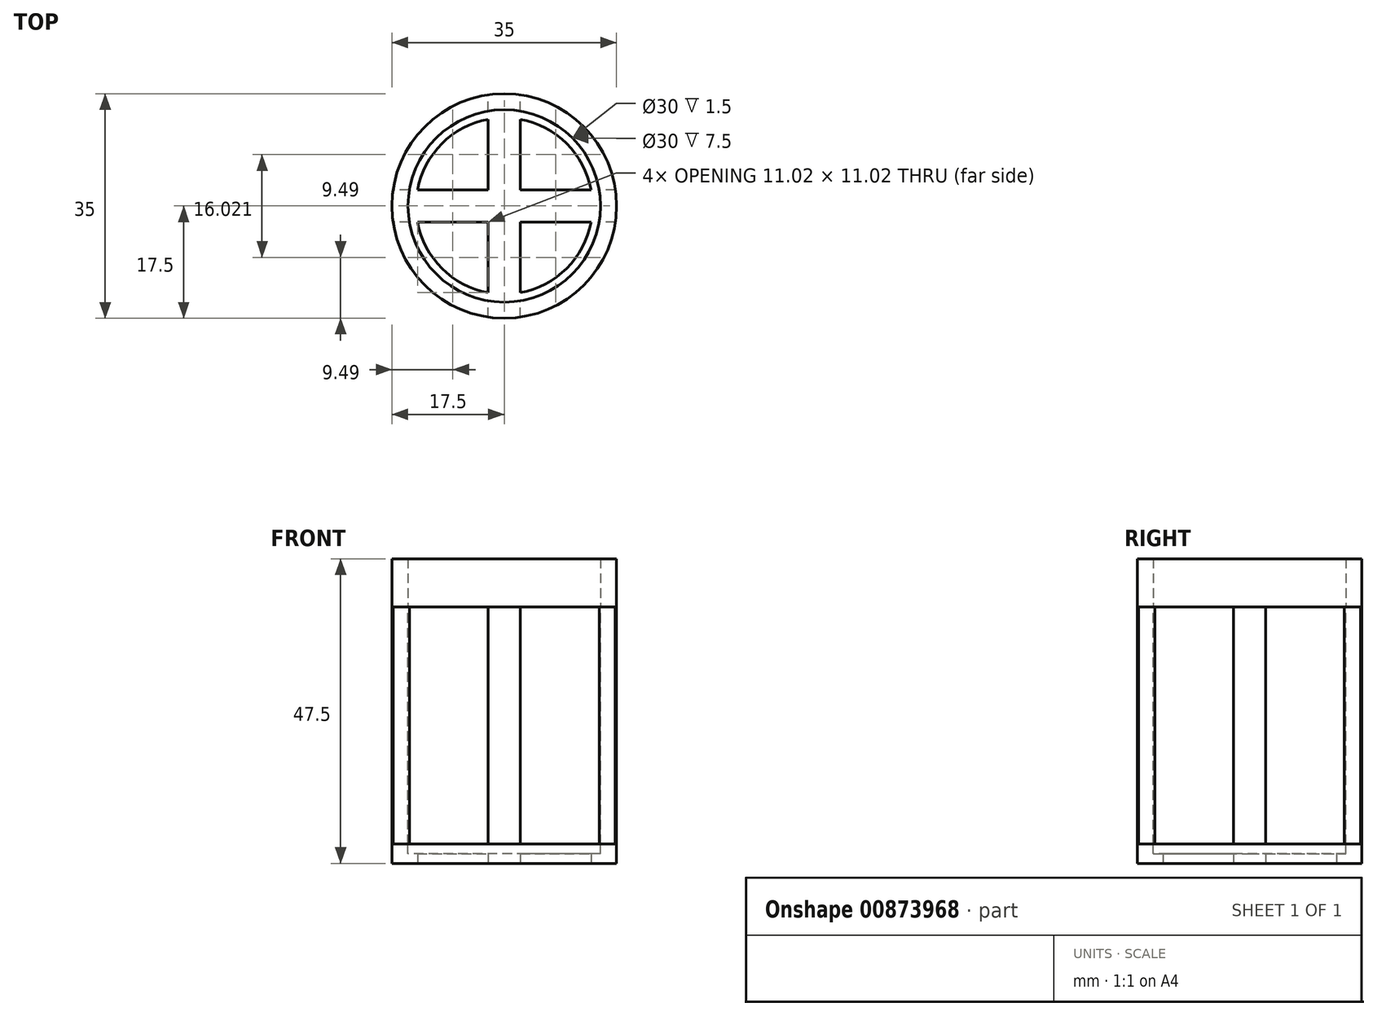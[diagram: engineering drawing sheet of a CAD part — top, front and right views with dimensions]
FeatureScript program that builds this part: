
annotation { "Feature Type Name" : "Feature", "Feature Type Description" : "" }
export const myFeature = defineFeature(function(context is Context, id is Id, definition is map)
    precondition{}
    {
        {
            var Q0;
            Q0=qCreatedBy(makeId("Top.planeOp"),FACE);
            var sketch = newSketch(context, id + "F0", { "sketchPlane" : qUnion([Q0])});
            skPoint(sketch, "E0.first.point", {"position": v(0, 0) * mm});
            skCircle(sketch, "E1", {"center": v(0, 0) * mm, "radius": 17.5 * mm});
            skCircle(sketch, "E2", {"center": v(0, 0) * mm, "radius": 13.75 * mm});
            skSolve(sketch);
        }
        {
            var Q0;
            Q0=makeQuery(id+"F0.imprint","IMPRINT",FACE,{"disambiguationData":[TD([[makeQuery(id+"F0.imprint","IMPRINT",EDGE,{"derivedFrom":sQuery(id+"F0.wireOp",EDGE,"E1")}),1.0]])]});
            extrude(context, id + "F1", {"entities" : qUnion([Q0]), "depth" : 43 * mm, "offsetDistance" : 25 * mm});
        }
        {
            var Q0;
            Q0=makeQuery(id+"F1.opExtrude","CAP_FACE",FACE,{"disambiguationData":[OSD([sQuery(id+"F0.wireOp",EDGE,"dMLi9CjI-w3AJ-lqrU-xDtC-pNT5ZKXLwRoQ"),sQuery(id+"F0.wireOp",EDGE,"p6jEfgZd-gn9l-At6D-uO4C-P7PHmhyGIQ6Y"),sQuery(id+"F0.wireOp",EDGE,"bsXDQPTp-62U9-H9b8-tNQK-BlYfqYmaa6Ta"),sQuery(id+"F0.wireOp",EDGE,"E1")])],"isStart":false});
            var sketch = newSketch(context, id + "F2", { "sketchPlane" : qUnion([Q0])});
            skCircle(sketch, "E3", {"center": v(0, 0) * mm, "radius": 15 * mm});
            skCircle(sketch, "E4", {"center": v(0, 0) * mm, "radius": 13.75 * mm});
            skSolve(sketch);
        }
        {
            var Q0;
            Q0 = qSketchRegion(id + "F2", true);
            extrude(context, id + "F3", {"entities" : qUnion([Q0]), "operationType" : NewBodyOperationType.REMOVE, "oppositeDirection" : true, "depth" : 41.5 * mm, "offsetDistance" : 25 * mm});
        }
        {
            var Q0;
            Q0=qCreatedBy(makeId("Top.planeOp"),FACE);
            cPlane(context, id + "F4", {"entities" : qUnion([Q0]), "cplaneType" : CPlaneType.OFFSET, "offset" : 3 * mm, "width" : 150 * mm, "height" : 150 * mm});
        }
        {
            var Q0;
            Q0=qCreatedBy(id+"F4.planeOp",FACE);
            var sketch = newSketch(context, id + "F5", { "sketchPlane" : qUnion([Q0])});
            skLineSegment(sketch, "E5.bottom", {"start": v(36.84, 2.5) * mm, "end": v(-36.84, 2.5) * mm});
            skLineSegment(sketch, "E5.top", {"start": v(36.84, -2.5) * mm, "end": v(-36.84, -2.5) * mm});
            skLineSegment(sketch, "E5.left", {"start": v(36.84, 2.5) * mm, "end": v(36.84, -2.5) * mm});
            skLineSegment(sketch, "E5.right", {"start": v(-36.84, 2.5) * mm, "end": v(-36.84, -2.5) * mm});
            skPoint(sketch, "E5.middle", {"position": v(0, 0) * mm});
            skLineSegment(sketch, "E6.bottom", {"start": v(2.5, -34.17) * mm, "end": v(-2.5, -34.17) * mm});
            skLineSegment(sketch, "E6.top", {"start": v(2.5, 34.17) * mm, "end": v(-2.5, 34.17) * mm});
            skLineSegment(sketch, "E6.left", {"start": v(2.5, -34.17) * mm, "end": v(2.5, 34.17) * mm});
            skLineSegment(sketch, "E6.right", {"start": v(-2.5, -34.17) * mm, "end": v(-2.5, 34.17) * mm});
            skSolve(sketch);
        }
        {
            var Q0;
            Q0 = qSketchRegion(id + "F5", true);
            extrude(context, id + "F6", {"entities" : qUnion([Q0]), "operationType" : NewBodyOperationType.INTERSECT, "depth" : 37 * mm, "offsetDistance" : 25 * mm});
        }
        {
            var Q0;
            Q0=qCreatedBy(makeId("Top.planeOp"),FACE);
            var sketch = newSketch(context, id + "F7", { "sketchPlane" : qUnion([Q0])});
            skCircle(sketch, "E7", {"center": v(0, 0) * mm, "radius": 17.5 * mm});
            skCircle(sketch, "E8", {"center": v(0, 0) * mm, "radius": 13.75 * mm});
            skSolve(sketch);
        }
        {
            var Q0;
            Q0 = qSketchRegion(id + "F7", true);
            extrude(context, id + "F8", {"entities" : qUnion([Q0]), "depth" : 3 * mm, "offsetDistance" : 25 * mm});
        }
        {
            var Q0;
            Q0=qCreatedBy(makeId("Top.planeOp"),FACE);
            cPlane(context, id + "F9", {"entities" : qUnion([Q0]), "cplaneType" : CPlaneType.OFFSET, "offset" : 40 * mm, "width" : 150 * mm, "height" : 150 * mm});
        }
        {
            var Q0;
            Q0=qCreatedBy(id+"F9.planeOp",FACE);
            var sketch = newSketch(context, id + "F10", { "sketchPlane" : qUnion([Q0])});
            skCircle(sketch, "E9", {"center": v(0, 0) * mm, "radius": 17.5 * mm});
            skCircle(sketch, "E10", {"center": v(0, 0) * mm, "radius": 15 * mm});
            skSolve(sketch);
        }
        {
            var Q0;
            Q0 = qSketchRegion(id + "F10", true);
            extrude(context, id + "F11", {"entities" : qUnion([Q0]), "depth" : 7.5 * mm, "offsetDistance" : 25 * mm});
        }
        {
            var Q0;
            Q0=makeQuery(id+"F8.opExtrude","CAP_FACE",FACE,{"disambiguationData":[OSD([sQuery(id+"F7.wireOp",EDGE,"E7"),sQuery(id+"F7.wireOp",EDGE,"E8")])],"isStart":false});
            var sketch = newSketch(context, id + "F12", { "sketchPlane" : qUnion([Q0])});
            skCircle(sketch, "E11", {"center": v(0, 0) * mm, "radius": 15 * mm});
            skSolve(sketch);
        }
        {
            var Q0;
            Q0 = qSketchRegion(id + "F12", true);
            extrude(context, id + "F13", {"entities" : qUnion([Q0]), "operationType" : NewBodyOperationType.REMOVE, "oppositeDirection" : true, "depth" : 1.5 * mm, "offsetDistance" : 25 * mm});
        }
        {
            var Q0;
            Q0=qCreatedBy(makeId("Top.planeOp"),FACE);
            var sketch = newSketch(context, id + "F14", { "sketchPlane" : qUnion([Q0])});
            skCircle(sketch, "E12", {"center": v(0, 0) * mm, "radius": 15 * mm});
            skLineSegment(sketch, "E13.bottom", {"start": v(-39.23, -2.5) * mm, "end": v(39.23, -2.5) * mm});
            skLineSegment(sketch, "E13.top", {"start": v(-39.23, 2.5) * mm, "end": v(39.23, 2.5) * mm});
            skLineSegment(sketch, "E13.left", {"start": v(-39.23, -2.5) * mm, "end": v(-39.23, 2.5) * mm});
            skLineSegment(sketch, "E13.right", {"start": v(39.23, -2.5) * mm, "end": v(39.23, 2.5) * mm});
            skLineSegment(sketch, "E14.bottom", {"start": v(-2.5, -39.25) * mm, "end": v(2.5, -39.25) * mm});
            skLineSegment(sketch, "E14.top", {"start": v(-2.5, 39.25) * mm, "end": v(2.5, 39.25) * mm});
            skLineSegment(sketch, "E14.left", {"start": v(-2.5, -39.25) * mm, "end": v(-2.5, 39.25) * mm});
            skLineSegment(sketch, "E14.right", {"start": v(2.5, -39.25) * mm, "end": v(2.5, 39.25) * mm});
            skSolve(sketch);
        }
        {
            var Q0;
            {var subQ0=sQuery(id+"F14.wireOp",EDGE,"E13.top");var subQ1=sQuery(id+"F14.wireOp",EDGE,"E12");var subQ2=makeQuery(id+"F14.imprint","INTERSECT",VERTEX,{"disambiguationData":[OD(0.0)],"derivedFrom":[subQ1,subQ0]});Q0=makeQuery(id+"F14.imprint","IMPRINT",FACE,{"disambiguationData":[TD([[makeQuery(id+"F14.imprint","IMPRINT",EDGE,{"disambiguationData":[TD([[subQ2,1.0]])],"derivedFrom":subQ1}),1.0]])]});}
            var Q1;
            {var subQ0=sQuery(id+"F14.wireOp",EDGE,"E14.left");var subQ1=sQuery(id+"F14.wireOp",EDGE,"E13.bottom");var subQ2=makeQuery(id+"F14.imprint","INTERSECT",VERTEX,{"derivedFrom":[subQ1,subQ0]});Q1=makeQuery(id+"F14.imprint","IMPRINT",FACE,{"disambiguationData":[TD([[makeQuery(id+"F14.imprint","IMPRINT",EDGE,{"disambiguationData":[TD([[subQ2,-1.0]])],"derivedFrom":subQ1}),1.0]])]});}
            var Q2;
            {var subQ0=sQuery(id+"F14.wireOp",EDGE,"E14.right");var subQ1=sQuery(id+"F14.wireOp",EDGE,"E12");var subQ2=makeQuery(id+"F14.imprint","INTERSECT",VERTEX,{"disambiguationData":[OD(0.0)],"derivedFrom":[subQ1,subQ0]});Q2=makeQuery(id+"F14.imprint","IMPRINT",FACE,{"disambiguationData":[TD([[makeQuery(id+"F14.imprint","IMPRINT",EDGE,{"disambiguationData":[TD([[subQ2,-1.0]])],"derivedFrom":subQ1}),1.0]])]});}
            var Q3;
            {var subQ0=sQuery(id+"F14.wireOp",EDGE,"E14.left");var subQ1=sQuery(id+"F14.wireOp",EDGE,"E12");var subQ2=makeQuery(id+"F14.imprint","INTERSECT",VERTEX,{"disambiguationData":[OD(1.0)],"derivedFrom":[subQ1,subQ0]});Q3=makeQuery(id+"F14.imprint","IMPRINT",FACE,{"disambiguationData":[TD([[makeQuery(id+"F14.imprint","IMPRINT",EDGE,{"disambiguationData":[TD([[subQ2,-1.0]])],"derivedFrom":subQ1}),1.0]])]});}
            var Q4;
            {var subQ0=sQuery(id+"F14.wireOp",EDGE,"E13.top");var subQ1=sQuery(id+"F14.wireOp",EDGE,"E12");var subQ2=makeQuery(id+"F14.imprint","INTERSECT",VERTEX,{"disambiguationData":[OD(1.0)],"derivedFrom":[subQ1,subQ0]});Q4=makeQuery(id+"F14.imprint","IMPRINT",FACE,{"disambiguationData":[TD([[makeQuery(id+"F14.imprint","IMPRINT",EDGE,{"disambiguationData":[TD([[subQ2,-1.0]])],"derivedFrom":subQ1}),1.0]])]});}
            extrude(context, id + "F15", {"entities" : qUnion([Q0, Q1, Q2, Q3, Q4]), "operationType" : NewBodyOperationType.ADD, "depth" : 1.5 * mm, "offsetDistance" : 25 * mm});
        }
    });
